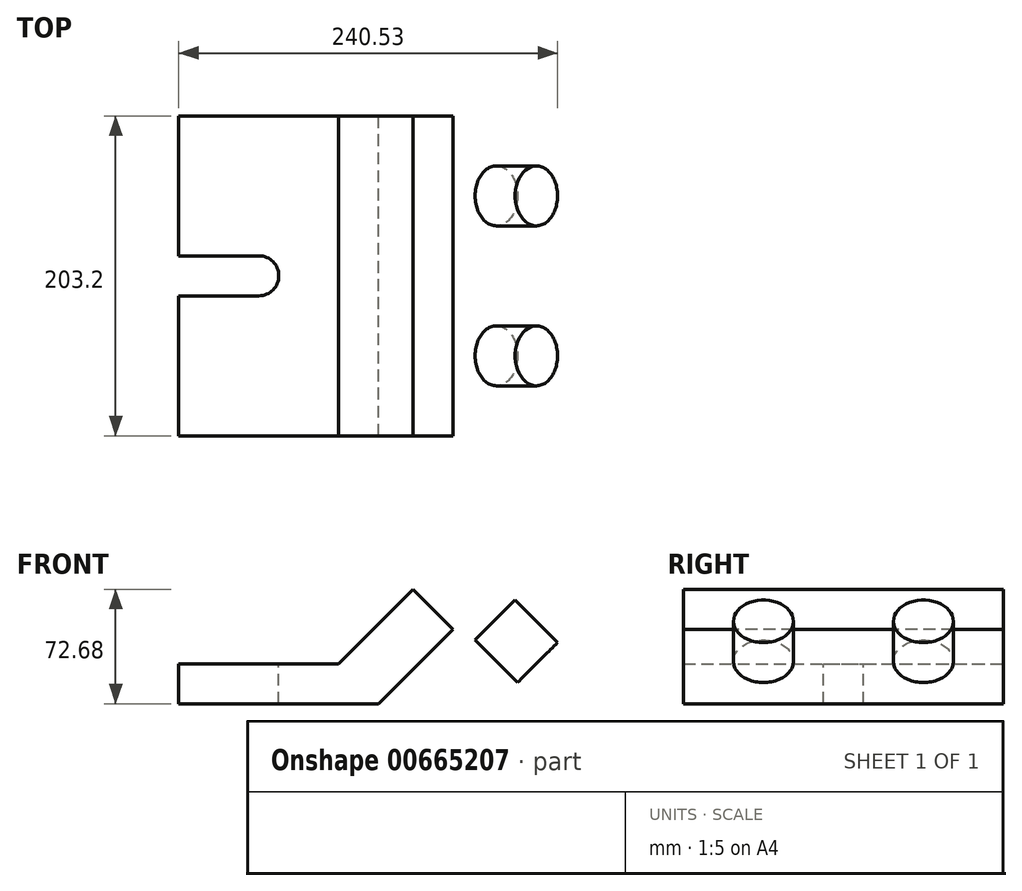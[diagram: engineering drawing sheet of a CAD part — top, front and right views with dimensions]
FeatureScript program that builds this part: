
annotation { "Feature Type Name" : "Feature", "Feature Type Description" : "" }
export const myFeature = defineFeature(function(context is Context, id is Id, definition is map)
    precondition{}
    {
        {
            var Q0;
            Q0=qCreatedBy(makeId("Front.planeOp"),FACE);
            var sketch = newSketch(context, id + "F0", { "sketchPlane" : qUnion([Q0])});
            skLineSegment(sketch, "E0", {"start": v(0, 0) * mm, "end": v(0, -25.4) * mm});
            skLineSegment(sketch, "E1", {"start": v(0, -25.4) * mm, "end": v(127, -25.4) * mm});
            skLineSegment(sketch, "E2", {"start": v(0, 0) * mm, "end": v(101.6, 0) * mm});
            skLineSegment(sketch, "E3", {"start": v(101.6, 0) * mm, "end": v(101.6, 50.8) * mm, "construction": true});
            skLineSegment(sketch, "E4", {"start": v(101.6, 50.8) * mm, "end": v(152.4, 50.8) * mm, "construction": true});
            skLineSegment(sketch, "E5", {"start": v(152.4, 50.8) * mm, "end": v(101.6, 0) * mm});
            skLineSegment(sketch, "E6", {"start": v(152.4, 50.8) * mm, "end": v(152.4, 101.6) * mm, "construction": true});
            skLineSegment(sketch, "E7", {"start": v(152.4, 101.6) * mm, "end": v(101.6, 101.6) * mm, "construction": true});
            skLineSegment(sketch, "E8", {"start": v(101.6, 101.6) * mm, "end": v(152.4, 50.8) * mm});
            skLineSegment(sketch, "E9", {"start": v(101.6, 101.6) * mm, "end": v(101.6, 127) * mm, "construction": true});
            skLineSegment(sketch, "E10", {"start": v(101.6, 127) * mm, "end": v(127, 127) * mm, "construction": true});
            skLineSegment(sketch, "E11", {"start": v(127, -25.4) * mm, "end": v(177.8, -25.4) * mm, "construction": true});
            skLineSegment(sketch, "E12", {"start": v(177.8, -25.4) * mm, "end": v(177.8, 25.4) * mm, "construction": true});
            skLineSegment(sketch, "E13", {"start": v(177.8, 25.4) * mm, "end": v(127, -25.4) * mm});
            skLineSegment(sketch, "E14", {"start": v(177.8, -25.4) * mm, "end": v(228.6, -25.4) * mm, "construction": true});
            skLineSegment(sketch, "E15", {"start": v(228.6, -25.4) * mm, "end": v(177.8, 25.4) * mm});
            skLineSegment(sketch, "E16", {"start": v(228.6, -25.4) * mm, "end": v(228.6, 0) * mm, "construction": true});
            skLineSegment(sketch, "E17", {"start": v(228.6, 0) * mm, "end": v(254, 0) * mm, "construction": true});
            skLineSegment(sketch, "E18", {"start": v(254, 0) * mm, "end": v(228.6, -25.4) * mm});
            skLineSegment(sketch, "E19", {"start": v(254, 0) * mm, "end": v(127, 127) * mm});
            skLineSegment(sketch, "E20", {"start": v(101.6, 101.6) * mm, "end": v(127, 127) * mm});
            skSolve(sketch);
        }
        {
            var Q0;
            Q0=makeQuery(id+"F0.imprint","IMPRINT",FACE,{"disambiguationData":[TD([[makeQuery(id+"F0.imprint","IMPRINT",EDGE,{"derivedFrom":sQuery(id+"F0.wireOp",EDGE,"E0")}),1.0]])]});
            extrude(context, id + "F1", {"entities" : qUnion([Q0]), "endBound" : BoundingType.SYMMETRIC, "depth" : 203.2 * mm, "offsetDistance" : 25.4 * mm});
        }
        {
            var Q0;
            Q0=makeQuery(id+"F1.opExtrude","SWEPT_FACE",FACE,{"disambiguationData":[OSD([sQuery(id+"F0.wireOp",EDGE,"E19")])]});
            var sketch = newSketch(context, id + "F2", { "sketchPlane" : qUnion([Q0])});
            skLineSegment(sketch, "E21.0", {"start": v(-101.6, -38.1) * mm, "end": v(-69.85, -38.1) * mm, "construction": true});
            skLineSegment(sketch, "E22.0", {"start": v(-50.8, -179.6) * mm, "end": v(-50.8, -38.1) * mm, "construction": true});
            skLineSegment(sketch, "E23.0", {"start": v(50.8, -179.6) * mm, "end": v(50.8, 0) * mm, "construction": true});
            skLineSegment(sketch, "E24", {"start": v(-101.6, -89.8) * mm, "end": v(101.6, -89.8) * mm, "construction": true});
            skCircle(sketch, "E25", {"center": v(-50.8, -38.1) * mm, "radius": 19.05 * mm});
            skCircle(sketch, "E26", {"center": v(50.8, -38.1) * mm, "radius": 19.05 * mm});
            skLineSegment(sketch, "E27", {"start": v(-50.8, -57.15) * mm, "end": v(50.8, -57.15) * mm});
            skLineSegment(sketch, "E28", {"start": v(-50.8, -19.05) * mm, "end": v(50.8, -19.05) * mm});
            skLineSegment(sketch, "E29.trimOffspring", {"start": v(-31.75, -38.1) * mm, "end": v(101.6, -38.1) * mm, "construction": true});
            skLineSegment(sketch, "E30.trimOffspring", {"start": v(-50.8, -19.05) * mm, "end": v(-50.8, 0) * mm, "construction": true});
            skCircle(sketch, "E31.MirrorC", {"center": v(-50.8, -141.5) * mm, "radius": 19.05 * mm});
            skCircle(sketch, "E32.MirrorC", {"center": v(50.8, -141.5) * mm, "radius": 19.05 * mm});
            skLineSegment(sketch, "E33.MirrorCS", {"start": v(-50.8, -122.46) * mm, "end": v(50.8, -122.46) * mm});
            skLineSegment(sketch, "E34.MirrorCS", {"start": v(-50.8, -160.56) * mm, "end": v(50.8, -160.56) * mm});
            skSolve(sketch);
        }
        {
            var Q0;
            {var subQ0=sQuery(id+"F2.wireOp",EDGE,"E27");Q0=makeQuery(id+"F2.imprint","IMPRINT",FACE,{"disambiguationData":[TD([[makeQuery(id+"F2.imprint","IMPRINT",EDGE,{"derivedFrom":subQ0}),1.0]])]});}
            var Q1;
            {var subQ0=sQuery(id+"F2.wireOp",EDGE,"E25");var subQ1=makeQuery(id+"F2.imprint","INTERSECT",VERTEX,{"derivedFrom":[subQ0,sQuery(id+"F2.wireOp",EDGE,"E27")]});Q1=makeQuery(id+"F2.imprint","IMPRINT",FACE,{"disambiguationData":[TD([[makeQuery(id+"F2.imprint","IMPRINT",EDGE,{"disambiguationData":[TD([[subQ1,1.0]])],"derivedFrom":subQ0}),1.0]])]});}
            var Q2;
            {var subQ0=sQuery(id+"F2.wireOp",EDGE,"E26");var subQ1=makeQuery(id+"F2.imprint","INTERSECT",VERTEX,{"derivedFrom":[subQ0,sQuery(id+"F2.wireOp",EDGE,"E27")]});Q2=makeQuery(id+"F2.imprint","IMPRINT",FACE,{"disambiguationData":[TD([[makeQuery(id+"F2.imprint","IMPRINT",EDGE,{"disambiguationData":[TD([[subQ1,1.0]])],"derivedFrom":subQ0}),1.0]])]});}
            var Q3;
            {var subQ0=sQuery(id+"F2.wireOp",EDGE,"E32.MirrorC");var subQ1=makeQuery(id+"F2.imprint","INTERSECT",VERTEX,{"derivedFrom":[subQ0,sQuery(id+"F2.wireOp",EDGE,"E33.MirrorCS")]});Q3=makeQuery(id+"F2.imprint","IMPRINT",FACE,{"disambiguationData":[TD([[makeQuery(id+"F2.imprint","IMPRINT",EDGE,{"disambiguationData":[TD([[subQ1,1.0]])],"derivedFrom":subQ0}),-1.0]])]});}
            var Q4;
            {var subQ0=sQuery(id+"F2.wireOp",EDGE,"E33.MirrorCS");Q4=makeQuery(id+"F2.imprint","IMPRINT",FACE,{"disambiguationData":[TD([[makeQuery(id+"F2.imprint","IMPRINT",EDGE,{"derivedFrom":subQ0}),-1.0]])]});}
            var Q5;
            {var subQ0=sQuery(id+"F2.wireOp",EDGE,"E31.MirrorC");var subQ1=makeQuery(id+"F2.imprint","INTERSECT",VERTEX,{"derivedFrom":[subQ0,sQuery(id+"F2.wireOp",EDGE,"E33.MirrorCS")]});Q5=makeQuery(id+"F2.imprint","IMPRINT",FACE,{"disambiguationData":[TD([[makeQuery(id+"F2.imprint","IMPRINT",EDGE,{"disambiguationData":[TD([[subQ1,1.0]])],"derivedFrom":subQ0}),-1.0]])]});}
            extrude(context, id + "F3", {"entities" : qUnion([Q0, Q1, Q2, Q3, Q4, Q5]), "operationType" : NewBodyOperationType.REMOVE, "oppositeDirection" : true, "depth" : 40.9 * mm, "offsetDistance" : 25.4 * mm});
        }
        {
            var Q0;
            Q0=makeQuery(id+"F1.opExtrude","SWEPT_FACE",FACE,{"disambiguationData":[OSD([sQuery(id+"F0.wireOp",EDGE,"E2")])]});
            var sketch = newSketch(context, id + "F4", { "sketchPlane" : qUnion([Q0])});
            skLineSegment(sketch, "E35", {"start": v(0, 0) * mm, "end": v(50.8, 0) * mm});
            skArc(sketch, "E36", {"start": v(50.8, -12.7) * mm, "mid": v(63.5, 0) * mm, "end": v(50.8, 12.7) * mm});
            skLineSegment(sketch, "E37", {"start": v(50.8, 12.7) * mm, "end": v(0, 12.7) * mm});
            skLineSegment(sketch, "E38", {"start": v(50.8, -12.7) * mm, "end": v(0, -12.7) * mm});
            skSolve(sketch);
        }
        {
            var Q0;
            Q0=makeQuery(id+"F4.imprint","IMPRINT",FACE,{"disambiguationData":[TD([[makeQuery(id+"F4.imprint","IMPRINT",EDGE,{"derivedFrom":sQuery(id+"F4.wireOp",EDGE,"E36")}),1.0]])]});
            extrude(context, id + "F5", {"entities" : qUnion([Q0]), "operationType" : NewBodyOperationType.REMOVE, "endBound" : BoundingType.THROUGH_ALL, "oppositeDirection" : true, "depth" : 25.4 * mm, "offsetDistance" : 25.4 * mm});
        }
    });
